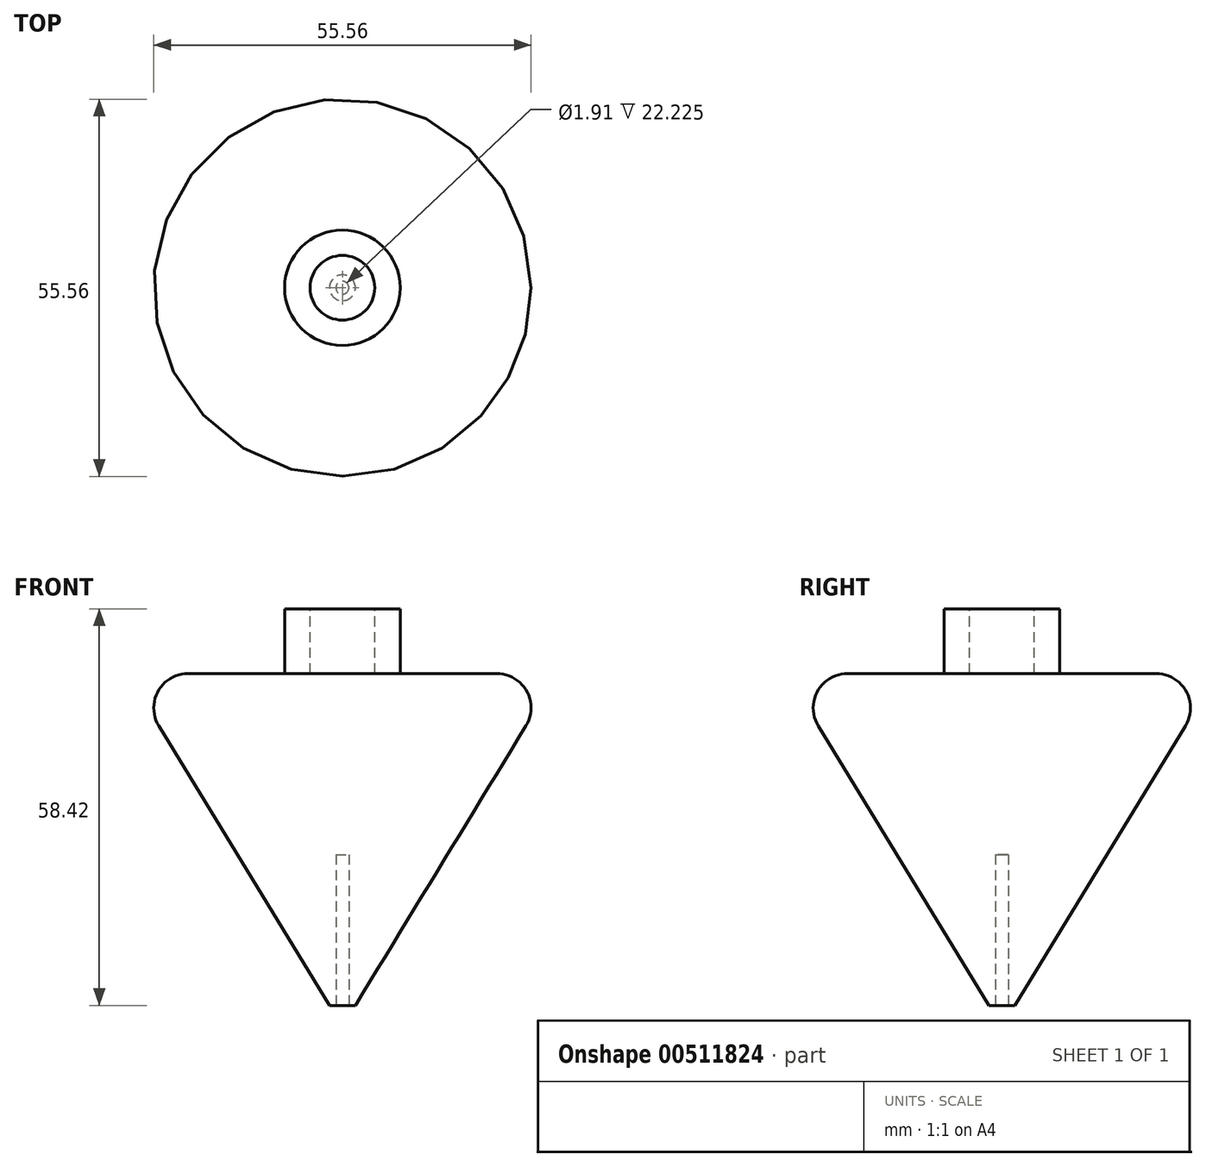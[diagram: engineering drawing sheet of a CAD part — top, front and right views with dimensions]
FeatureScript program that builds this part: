
annotation { "Feature Type Name" : "Feature", "Feature Type Description" : "" }
export const myFeature = defineFeature(function(context is Context, id is Id, definition is map)
    precondition{}
    {
        {
            var Q0;
            Q0=qCreatedBy(makeId("Front.planeOp"),FACE);
            var sketch = newSketch(context, id + "F0", { "sketchPlane" : qUnion([Q0])});
            skLineSegment(sketch, "E0", {"start": v(0, 0) * mm, "end": v(1.9, 0) * mm});
            skLineSegment(sketch, "E1", {"start": v(1.9, 0) * mm, "end": v(27.03, 41.17) * mm});
            skLineSegment(sketch, "E2", {"start": v(22.7, 48.9) * mm, "end": v(8.5, 48.9) * mm});
            skLineSegment(sketch, "E3", {"start": v(8.5, 48.9) * mm, "end": v(8.5, 58.42) * mm});
            skLineSegment(sketch, "E4", {"start": v(8.5, 58.42) * mm, "end": v(0, 58.42) * mm});
            skLineSegment(sketch, "E5", {"start": v(0, 58.42) * mm, "end": v(0, 0) * mm});
            skPoint(sketch, "E6.visualSharp", {"position": v(31.75, 48.9) * mm});
            skArc(sketch, "E6.filletArc", {"start": v(27.03, 41.17) * mm, "mid": v(27.13, 46.3) * mm, "end": v(22.7, 48.9) * mm});
            skSolve(sketch);
        }
        {
            var Q0;
            Q0=makeQuery(id+"F0.imprint","IMPRINT",FACE,{"disambiguationData":[TD([[makeQuery(id+"F0.imprint","IMPRINT",EDGE,{"derivedFrom":sQuery(id+"F0.wireOp",EDGE,"E0")}),1.0]])]});
            var Q1;
            Q1=sQuery(id+"F0.wireOp",EDGE,"E5");
            revolve(context, id + "F1", {"entities" : qUnion([Q0]), "axis" : qUnion([Q1]), "revolveType" : RevolveType.FULL});
        }
        {
            var Q0;
            Q0=makeQuery(id+"F1.opRevolve","SWEPT_FACE",FACE,{"disambiguationData":[OSD([sQuery(id+"F0.wireOp",EDGE,"E4")])]});
            var sketch = newSketch(context, id + "F2", { "sketchPlane" : qUnion([Q0])});
            skCircle(sketch, "E7", {"center": v(0, 0) * mm, "radius": 4.76 * mm});
            skSolve(sketch);
        }
        {
            var Q0;
            Q0=makeQuery(id+"F2.imprint","IMPRINT",FACE,{"disambiguationData":[TD([[makeQuery(id+"F2.imprint","IMPRINT",EDGE,{"derivedFrom":sQuery(id+"F2.wireOp",EDGE,"E7")}),1.0]])]});
            extrude(context, id + "F3", {"entities" : qUnion([Q0]), "operationType" : NewBodyOperationType.REMOVE, "oppositeDirection" : true, "depth" : 9.52 * mm});
        }
        {
            var Q0;
            Q0=makeQuery(id+"F1.opRevolve","SWEPT_FACE",FACE,{"disambiguationData":[OSD([sQuery(id+"F0.wireOp",EDGE,"E0")])]});
            var sketch = newSketch(context, id + "F4", { "sketchPlane" : qUnion([Q0])});
            skCircle(sketch, "E8", {"center": v(0, 0) * mm, "radius": 0.95 * mm});
            skSolve(sketch);
        }
        {
            var Q0;
            Q0 = qSketchRegion(id + "F4", true);
            extrude(context, id + "F5", {"entities" : qUnion([Q0]), "operationType" : NewBodyOperationType.REMOVE, "oppositeDirection" : true, "depth" : 22.22 * mm});
        }
    });
